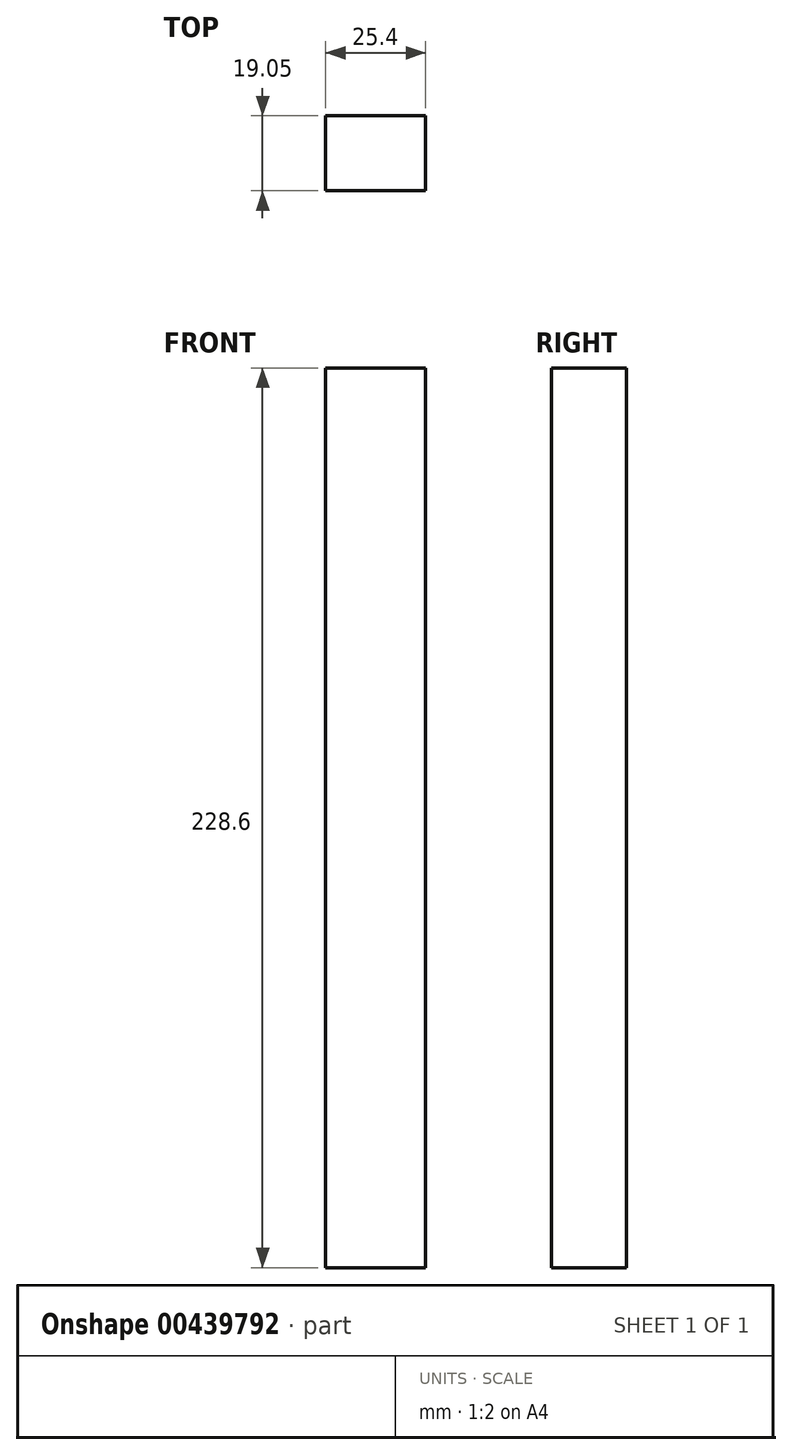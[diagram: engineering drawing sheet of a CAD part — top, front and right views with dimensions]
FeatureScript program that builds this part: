
annotation { "Feature Type Name" : "Feature", "Feature Type Description" : "" }
export const myFeature = defineFeature(function(context is Context, id is Id, definition is map)
    precondition{}
    {
        {
            var Q0;
            Q0=qCreatedBy(makeId("Front.planeOp"),FACE);
            var sketch = newSketch(context, id + "F0", { "sketchPlane" : qUnion([Q0])});
            skLineSegment(sketch, "E0.bottom", {"start": v(12.7, -114.3) * mm, "end": v(-12.7, -114.3) * mm});
            skLineSegment(sketch, "E0.top", {"start": v(12.7, 114.3) * mm, "end": v(-12.7, 114.3) * mm});
            skLineSegment(sketch, "E0.left", {"start": v(12.7, -114.3) * mm, "end": v(12.7, 114.3) * mm});
            skLineSegment(sketch, "E0.right", {"start": v(-12.7, -114.3) * mm, "end": v(-12.7, 114.3) * mm});
            skPoint(sketch, "E0.middle", {"position": v(0, 0) * mm});
            skSolve(sketch);
        }
        {
            var Q0;
            Q0=makeQuery(id+"F0.imprint","IMPRINT",FACE,{"disambiguationData":[TD([[makeQuery(id+"F0.imprint","IMPRINT",EDGE,{"derivedFrom":sQuery(id+"F0.wireOp",EDGE,"E0.bottom")}),-1.0]])]});
            extrude(context, id + "F1", {"entities" : qUnion([Q0]), "depth" : 19.05 * mm});
        }
    });
